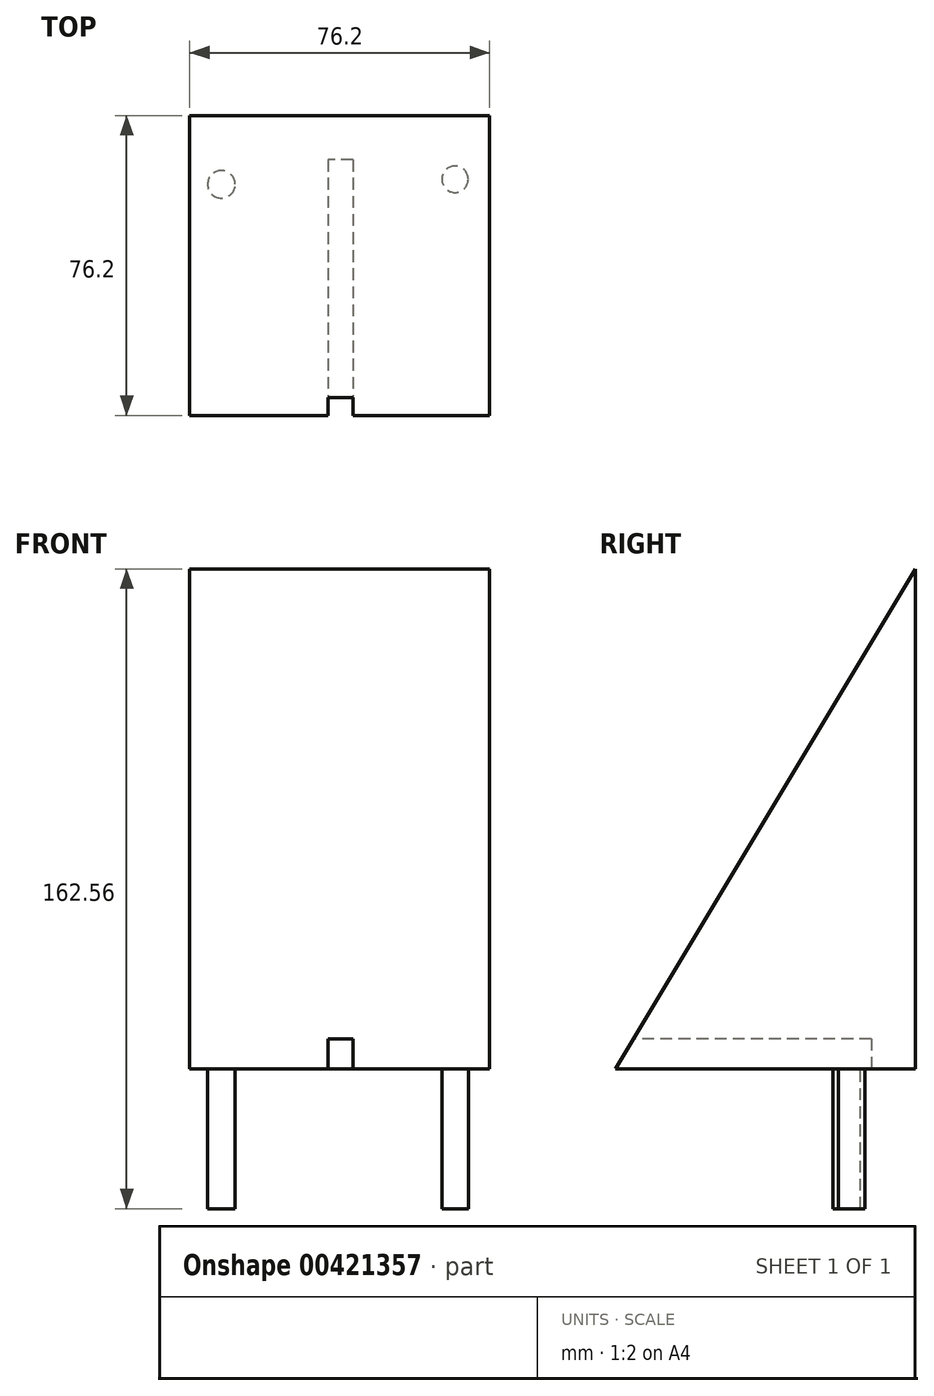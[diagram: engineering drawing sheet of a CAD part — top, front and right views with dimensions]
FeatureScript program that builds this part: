
annotation { "Feature Type Name" : "Feature", "Feature Type Description" : "" }
export const myFeature = defineFeature(function(context is Context, id is Id, definition is map)
    precondition{}
    {
        {
            var Q0;
            Q0=qCreatedBy(makeId("Right.planeOp"),FACE);
            var sketch = newSketch(context, id + "F0", { "sketchPlane" : qUnion([Q0])});
            skLineSegment(sketch, "E0", {"start": v(-29.28, 0) * mm, "end": v(46.92, 127) * mm});
            skLineSegment(sketch, "E1", {"start": v(46.92, 127) * mm, "end": v(46.92, 0) * mm});
            skLineSegment(sketch, "E2", {"start": v(46.92, 0) * mm, "end": v(-29.28, 0) * mm});
            skSolve(sketch);
        }
        {
            var Q0;
            Q0 = qSketchRegion(id + "F0", true);
            extrude(context, id + "F1", {"entities" : qUnion([Q0]), "depth" : 76.2 * mm});
        }
        {
            var Q0;
            Q0=makeQuery(id+"F1.opExtrude","SWEPT_FACE",FACE,{"disambiguationData":[OSD([sQuery(id+"F0.wireOp",EDGE,"E2")])]});
            var sketch = newSketch(context, id + "F2", { "sketchPlane" : qUnion([Q0])});
            skLineSegment(sketch, "E3.bottom", {"start": v(41.45, -35.68) * mm, "end": v(35.1, -35.68) * mm});
            skLineSegment(sketch, "E3.top", {"start": v(41.45, 48.14) * mm, "end": v(35.1, 48.14) * mm});
            skLineSegment(sketch, "E3.left", {"start": v(41.45, -35.68) * mm, "end": v(41.45, 48.14) * mm});
            skLineSegment(sketch, "E3.right", {"start": v(35.1, -35.68) * mm, "end": v(35.1, 48.14) * mm});
            skLineSegment(sketch, "E4", {"start": v(38.1, 29.28) * mm, "end": v(38.1, -46.92) * mm});
            skSolve(sketch);
        }
        {
            var Q0;
            Q0=makeQuery(id+"F2.imprint","IMPRINT",FACE,{"disambiguationData":[TD([[makeQuery(id+"F2.imprint","IMPRINT",EDGE,{"derivedFrom":sQuery(id+"F2.wireOp",EDGE,"E3.bottom")}),-1.0]])]});
            extrude(context, id + "F3", {"entities" : qUnion([Q0]), "operationType" : NewBodyOperationType.REMOVE, "oppositeDirection" : true, "depth" : 7.62 * mm});
        }
        {
            var Q0;
            Q0=makeQuery(id+"F1.opExtrude","SWEPT_FACE",FACE,{"disambiguationData":[OSD([sQuery(id+"F0.wireOp",EDGE,"E2")])]});
            var sketch = newSketch(context, id + "F4", { "sketchPlane" : qUnion([Q0])});
            skCircle(sketch, "E5", {"center": v(8.03, -29.4) * mm, "radius": 3.5 * mm});
            skCircle(sketch, "E6", {"center": v(67.38, -30.7) * mm, "radius": 3.37 * mm});
            skSolve(sketch);
        }
        {
            var Q0;
            Q0=makeQuery(id+"F4.imprint","IMPRINT",FACE,{"disambiguationData":[TD([[makeQuery(id+"F4.imprint","IMPRINT",EDGE,{"derivedFrom":sQuery(id+"F4.wireOp",EDGE,"E5")}),1.0]])]});
            var sketch = newSketch(context, id + "F5", { "sketchPlane" : qUnion([Q0])});
            skSolve(sketch);
        }
        {
            var Q0;
            Q0 = qSketchRegion(id + "F5", true);
            var Q1;
            Q1=makeQuery(id+"F4.imprint","IMPRINT",FACE,{"disambiguationData":[TD([[makeQuery(id+"F4.imprint","IMPRINT",EDGE,{"derivedFrom":sQuery(id+"F4.wireOp",EDGE,"E6")}),1.0]])]});
            extrude(context, id + "F6", {"entities" : qUnion([Q0, Q1]), "operationType" : NewBodyOperationType.ADD, "depth" : 35.56 * mm});
        }
        {
            var Q0;
            Q0=makeQuery(id+"F5.imprint","IMPRINT",FACE,{"disambiguationData":[TD([[makeQuery(id+"F5.imprint","IMPRINT",EDGE,{"derivedFrom":makeQuery(id+"F4.imprint","IMPRINT",EDGE,{"derivedFrom":sQuery(id+"F4.wireOp",EDGE,"E5")})}),1.0]])]});
            extrude(context, id + "F7", {"entities" : qUnion([Q0]), "operationType" : NewBodyOperationType.ADD, "depth" : 35.56 * mm});
        }
    });
